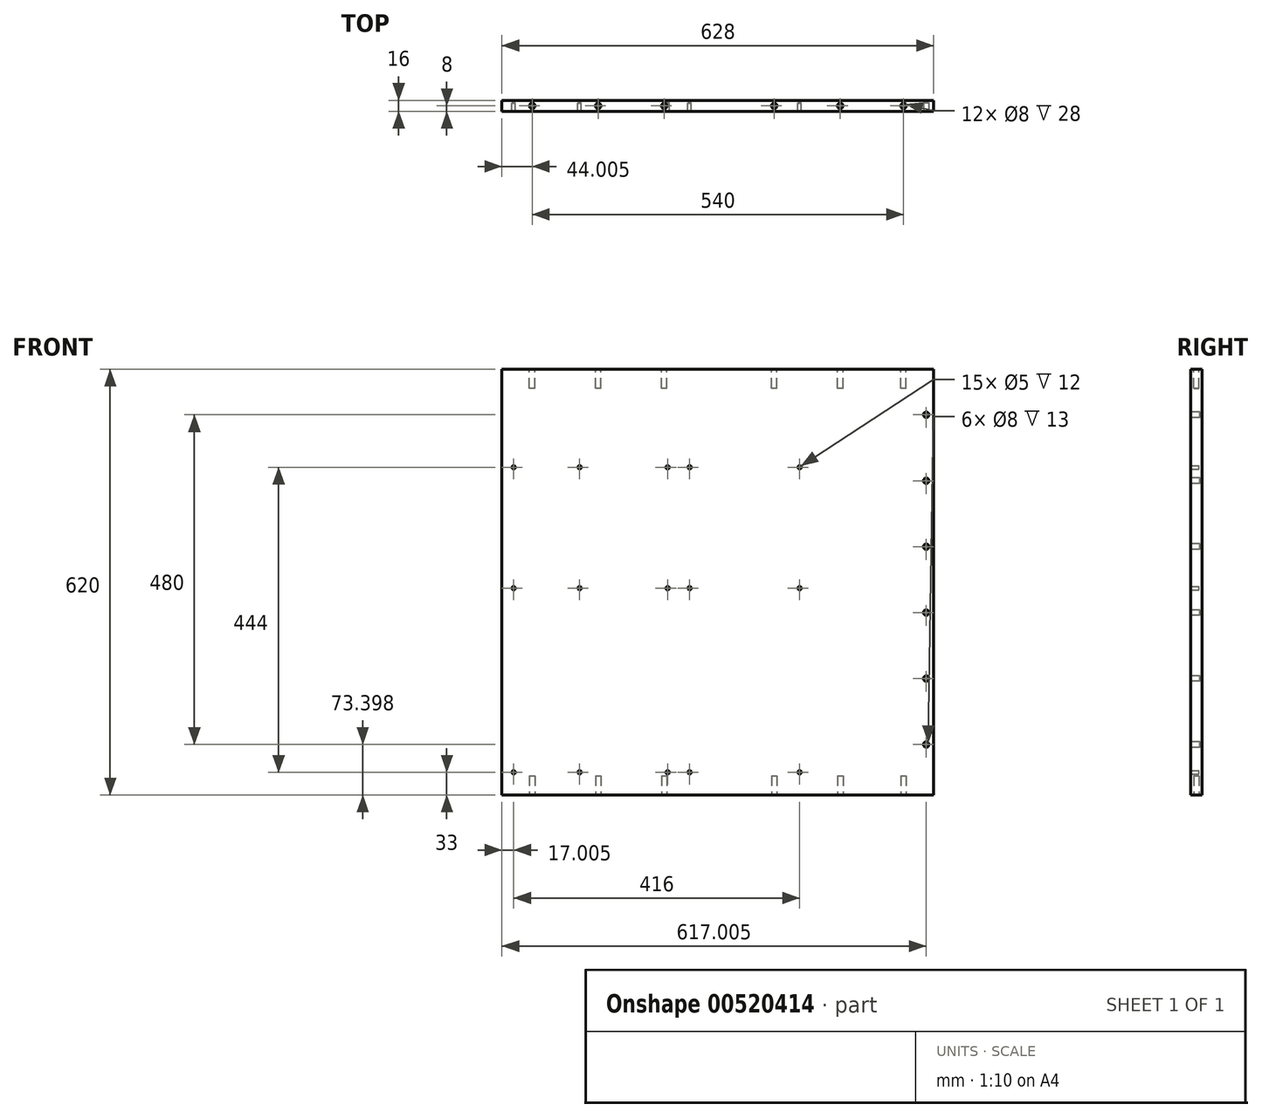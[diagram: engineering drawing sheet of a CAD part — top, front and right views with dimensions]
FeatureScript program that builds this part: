
annotation { "Feature Type Name" : "Feature", "Feature Type Description" : "" }
export const myFeature = defineFeature(function(context is Context, id is Id, definition is map)
    precondition{}
    {
        {
            var Q0;
            Q0=qCreatedBy(makeId("Top.planeOp"),FACE);
            var sketch = newSketch(context, id + "F0", { "sketchPlane" : qUnion([Q0])});
            skLineSegment(sketch, "E0.bottom", {"start": v(320.24, 8) * mm, "end": v(-307.76, 8) * mm});
            skLineSegment(sketch, "E0.top", {"start": v(320.24, -8) * mm, "end": v(-307.76, -8) * mm});
            skLineSegment(sketch, "E0.left", {"start": v(320.24, 8) * mm, "end": v(320.24, -8) * mm});
            skLineSegment(sketch, "E0.right", {"start": v(-307.76, 8) * mm, "end": v(-307.76, -8) * mm});
            skPoint(sketch, "E0.middle", {"position": v(6.24, 0) * mm});
            skSolve(sketch);
        }
        {
            var Q0;
            Q0 = qSketchRegion(id + "F0", true);
            extrude(context, id + "F1", {"entities" : qUnion([Q0]), "depth" : 620 * mm, "offsetDistance" : 25 * mm});
        }
        {
            var Q0;
            Q0=makeQuery(id+"F1.opExtrude","CAP_FACE",FACE,{"disambiguationData":[OSD([sQuery(id+"F0.wireOp",EDGE,"E0.bottom"),sQuery(id+"F0.wireOp",EDGE,"E0.top"),sQuery(id+"F0.wireOp",EDGE,"E0.left"),sQuery(id+"F0.wireOp",EDGE,"E0.right")])],"isStart":true});
            var sketch = newSketch(context, id + "F2", { "sketchPlane" : qUnion([Q0])});
            skLineSegment(sketch, "E1", {"start": v(-263.76, 0) * mm, "end": v(276.24, 0) * mm, "construction": true});
            skCircle(sketch, "E2", {"center": v(-263.76, 0) * mm, "radius": 4 * mm});
            skCircle(sketch, "E3", {"center": v(-167.76, 0) * mm, "radius": 4 * mm});
            skCircle(sketch, "E4", {"center": v(-71.76, 0) * mm, "radius": 4 * mm});
            skCircle(sketch, "E5", {"center": v(88.24, 0) * mm, "radius": 4 * mm});
            skCircle(sketch, "E6", {"center": v(276.24, 0) * mm, "radius": 4 * mm});
            skCircle(sketch, "E7", {"center": v(184.24, 0) * mm, "radius": 4 * mm});
            skLineSegment(sketch, "E8", {"start": v(6.24, 8) * mm, "end": v(6.24, 0) * mm, "construction": true});
            skSolve(sketch);
        }
        {
            var Q0;
            Q0 = qSketchRegion(id + "F2", true);
            extrude(context, id + "F3", {"entities" : qUnion([Q0]), "operationType" : NewBodyOperationType.REMOVE, "oppositeDirection" : true, "depth" : 28 * mm, "offsetDistance" : 25 * mm});
        }
        {
            var Q0;
            Q0=makeQuery(id+"F1.opExtrude","CAP_FACE",FACE,{"disambiguationData":[OSD([sQuery(id+"F0.wireOp",EDGE,"E0.bottom"),sQuery(id+"F0.wireOp",EDGE,"E0.top"),sQuery(id+"F0.wireOp",EDGE,"E0.left"),sQuery(id+"F0.wireOp",EDGE,"E0.right")])],"isStart":false});
            var sketch = newSketch(context, id + "F4", { "sketchPlane" : qUnion([Q0])});
            skLineSegment(sketch, "E9.1", {"start": v(-263.76, 0) * mm, "end": v(276.24, 0) * mm, "construction": true});
            skCircle(sketch, "E9.2", {"center": v(-263.76, 0) * mm, "radius": 4 * mm});
            skCircle(sketch, "E9.3", {"center": v(-167.76, 0) * mm, "radius": 4 * mm});
            skCircle(sketch, "E9.4", {"center": v(-71.76, 0) * mm, "radius": 4 * mm});
            skCircle(sketch, "E9.5", {"center": v(88.24, 0) * mm, "radius": 4 * mm});
            skCircle(sketch, "E9.6", {"center": v(276.24, 0) * mm, "radius": 4 * mm});
            skCircle(sketch, "E9.7", {"center": v(184.24, 0) * mm, "radius": 4 * mm});
            skSolve(sketch);
        }
        {
            var Q0;
            Q0 = qSketchRegion(id + "F4", true);
            extrude(context, id + "F5", {"entities" : qUnion([Q0]), "operationType" : NewBodyOperationType.REMOVE, "oppositeDirection" : true, "depth" : 28 * mm, "offsetDistance" : 25 * mm});
        }
        {
            var Q0;
            Q0=qCreatedBy(makeId("Front.planeOp"),FACE);
            var sketch = newSketch(context, id + "F6", { "sketchPlane" : qUnion([Q0])});
            skLineSegment(sketch, "E10", {"start": v(-290.76, 33) * mm, "end": v(-98.76, 33) * mm, "construction": true});
            skCircle(sketch, "E11", {"center": v(-290.76, 33) * mm, "radius": 2.5 * mm});
            skCircle(sketch, "E12", {"center": v(-66.76, 33) * mm, "radius": 2.5 * mm});
            skCircle(sketch, "E13", {"center": v(-194.76, 33) * mm, "radius": 2.5 * mm});
            skCircle(sketch, "E14", {"center": v(-34.76, 33) * mm, "radius": 2.5 * mm});
            skCircle(sketch, "E15", {"center": v(125.24, 33) * mm, "radius": 2.5 * mm});
            skLineSegment(sketch, "E16.0.1.0", {"start": v(-290.76, 301) * mm, "end": v(-98.76, 301) * mm, "construction": true});
            skCircle(sketch, "E16.0.1.1", {"center": v(125.24, 301) * mm, "radius": 2.5 * mm});
            skCircle(sketch, "E16.0.1.2", {"center": v(-34.76, 301) * mm, "radius": 2.5 * mm});
            skCircle(sketch, "E16.0.1.3", {"center": v(-194.76, 301) * mm, "radius": 2.5 * mm});
            skCircle(sketch, "E16.0.1.4", {"center": v(-66.76, 301) * mm, "radius": 2.5 * mm});
            skCircle(sketch, "E16.0.1.5", {"center": v(-290.76, 301) * mm, "radius": 2.5 * mm});
            skLineSegment(sketch, "E16.direction1", {"start": v(-290.76, 33) * mm, "end": v(-271.76, 33) * mm, "construction": true});
            skLineSegment(sketch, "E16.direction2", {"start": v(-290.76, 33) * mm, "end": v(-290.76, 301) * mm, "construction": true});
            skLineSegment(sketch, "E17.0.1.0", {"start": v(-290.76, 477) * mm, "end": v(-98.76, 477) * mm, "construction": true});
            skCircle(sketch, "E17.0.1.1", {"center": v(125.24, 477) * mm, "radius": 2.5 * mm});
            skCircle(sketch, "E17.0.1.2", {"center": v(-34.76, 477) * mm, "radius": 2.5 * mm});
            skCircle(sketch, "E17.0.1.3", {"center": v(-194.76, 477) * mm, "radius": 2.5 * mm});
            skCircle(sketch, "E17.0.1.4", {"center": v(-66.76, 477) * mm, "radius": 2.5 * mm});
            skCircle(sketch, "E17.0.1.5", {"center": v(-290.76, 477) * mm, "radius": 2.5 * mm});
            skLineSegment(sketch, "E17.direction1", {"start": v(-290.76, 301) * mm, "end": v(-265.76, 301) * mm, "construction": true});
            skLineSegment(sketch, "E17.direction2", {"start": v(-290.76, 301) * mm, "end": v(-290.76, 477) * mm, "construction": true});
            skSolve(sketch);
        }
        {
            var Q0;
            Q0 = qSketchRegion(id + "F6", true);
            extrude(context, id + "F7", {"entities" : qUnion([Q0]), "operationType" : NewBodyOperationType.REMOVE, "endBound" : BoundingType.UP_TO_NEXT, "depth" : 14 * mm, "offsetDistance" : 25 * mm, "hasSecondDirection" : true, "secondDirectionOppositeDirection" : true, "secondDirectionDepth" : 4 * mm});
        }
        {
            var Q0;
            Q0=makeQuery(id+"F1.opExtrude","SWEPT_FACE",FACE,{"disambiguationData":[OSD([sQuery(id+"F0.wireOp",EDGE,"E0.top")])]});
            var sketch = newSketch(context, id + "F8", { "sketchPlane" : qUnion([Q0])});
            skLineSegment(sketch, "E18", {"start": v(309.24, 553.4) * mm, "end": v(309.24, 66.6) * mm, "construction": true});
            skLineSegment(sketch, "E19", {"start": v(320.24, 310) * mm, "end": v(309.24, 310) * mm, "construction": true});
            skCircle(sketch, "E20", {"center": v(309.24, 553.4) * mm, "radius": 4 * mm});
            skCircle(sketch, "E21.0.1.0", {"center": v(309.24, 521.4) * mm, "radius": 4 * mm, "construction": true});
            skCircle(sketch, "E21.0.2.0", {"center": v(309.24, 489.4) * mm, "radius": 4 * mm, "construction": true});
            skCircle(sketch, "E21.0.3.0", {"center": v(309.24, 457.4) * mm, "radius": 4 * mm});
            skCircle(sketch, "E21.0.4.0", {"center": v(309.24, 425.4) * mm, "radius": 4 * mm, "construction": true});
            skCircle(sketch, "E21.0.5.0", {"center": v(309.24, 393.4) * mm, "radius": 4 * mm, "construction": true});
            skCircle(sketch, "E21.0.6.0", {"center": v(309.24, 361.4) * mm, "radius": 4 * mm});
            skCircle(sketch, "E21.0.7.0", {"center": v(309.24, 329.4) * mm, "radius": 4 * mm, "construction": true});
            skCircle(sketch, "E21.0.8.0", {"center": v(309.24, 297.4) * mm, "radius": 4 * mm, "construction": true});
            skCircle(sketch, "E21.0.9.0", {"center": v(309.24, 265.4) * mm, "radius": 4 * mm});
            skCircle(sketch, "E21.0.10.0", {"center": v(309.24, 233.4) * mm, "radius": 4 * mm, "construction": true});
            skCircle(sketch, "E21.0.11.0", {"center": v(309.24, 201.4) * mm, "radius": 4 * mm, "construction": true});
            skCircle(sketch, "E21.0.12.0", {"center": v(309.24, 169.4) * mm, "radius": 4 * mm});
            skCircle(sketch, "E21.0.13.0", {"center": v(309.24, 137.4) * mm, "radius": 4 * mm, "construction": true});
            skCircle(sketch, "E21.0.14.0", {"center": v(309.24, 105.4) * mm, "radius": 4 * mm, "construction": true});
            skCircle(sketch, "E21.0.15.0", {"center": v(309.24, 73.4) * mm, "radius": 4 * mm});
            skLineSegment(sketch, "E21.direction1", {"start": v(309.24, 553.4) * mm, "end": v(334.24, 553.4) * mm, "construction": true});
            skLineSegment(sketch, "E21.direction2", {"start": v(309.24, 553.4) * mm, "end": v(309.24, 521.4) * mm, "construction": true});
            skSolve(sketch);
        }
        {
            var Q0;
            Q0 = qSketchRegion(id + "F8", true);
            extrude(context, id + "F9", {"entities" : qUnion([Q0]), "operationType" : NewBodyOperationType.REMOVE, "oppositeDirection" : true, "depth" : 13 * mm, "offsetDistance" : 25 * mm});
        }
    });
